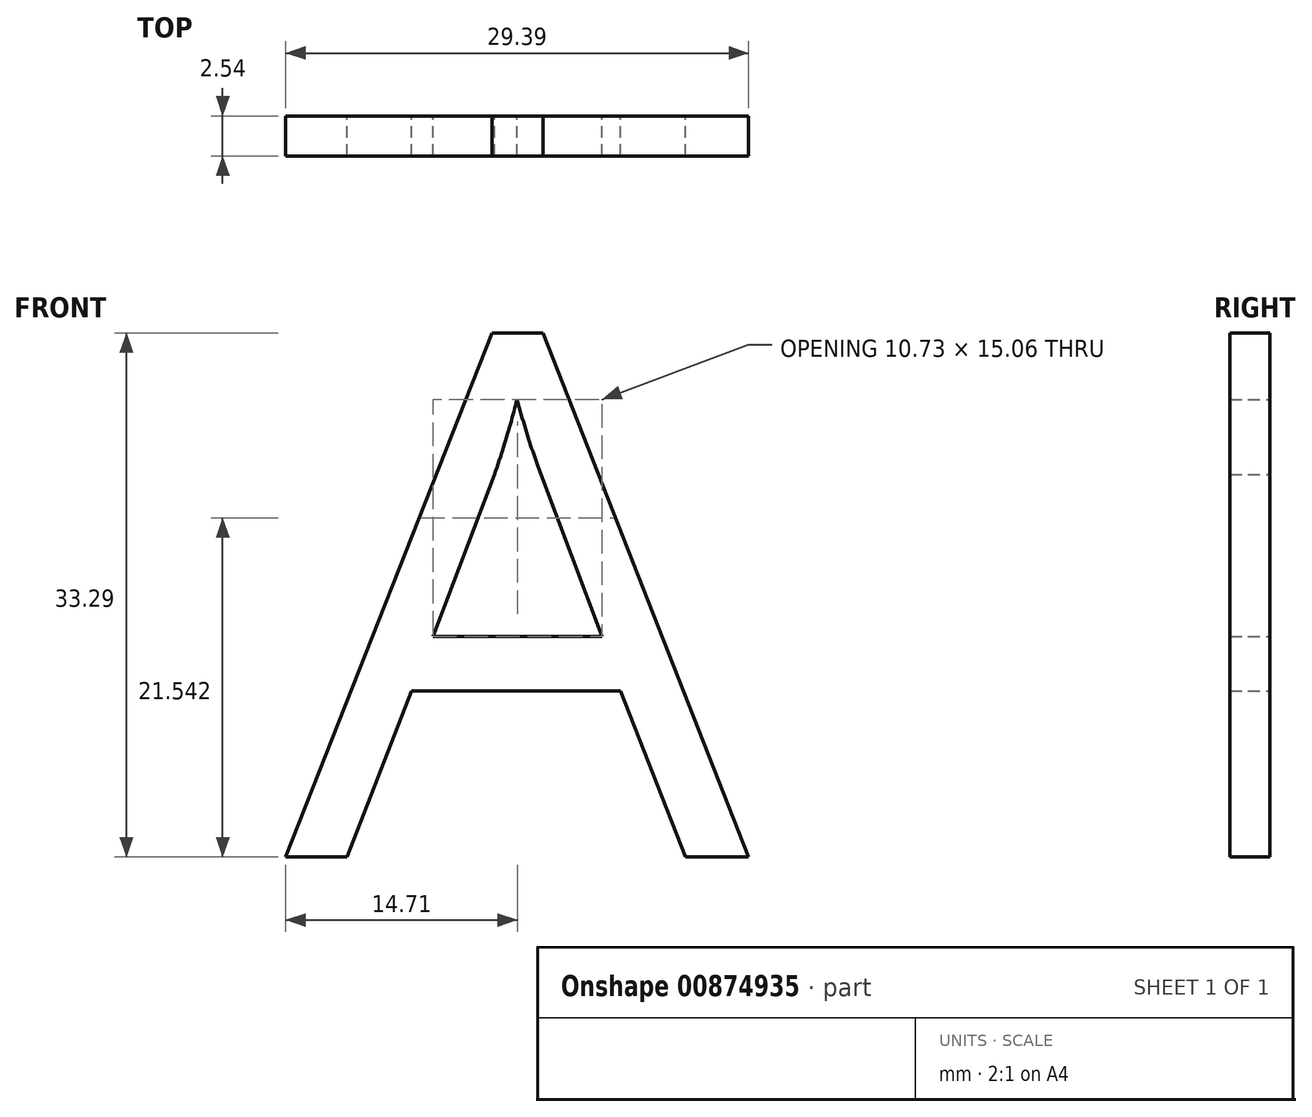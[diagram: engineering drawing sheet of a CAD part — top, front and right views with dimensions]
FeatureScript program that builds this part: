
annotation { "Feature Type Name" : "Feature", "Feature Type Description" : "" }
export const myFeature = defineFeature(function(context is Context, id is Id, definition is map)
    precondition{}
    {
        {
            var Q0;
            Q0=qCreatedBy(makeId("Front.planeOp"),FACE);
            var sketch = newSketch(context, id + "F0", { "sketchPlane" : qUnion([Q0])});
            skText(sketch, "E0", { "text": "A\n", "fontName": "OpenSans-Regular.ttf"});
            const initialGuessF0  = {"E0": [-0.0324, 0, 1, 0, 0.03344]};
            skSetInitialGuess(sketch, initialGuessF0);
            skSolve(sketch);
        }
        {
            var Q0;
            Q0 = qSketchRegion(id + "F0", true);
            extrude(context, id + "F1", {"entities" : qUnion([Q0]), "depth" : 2.54 * mm, "offsetDistance" : 25.4 * mm});
        }
    });
